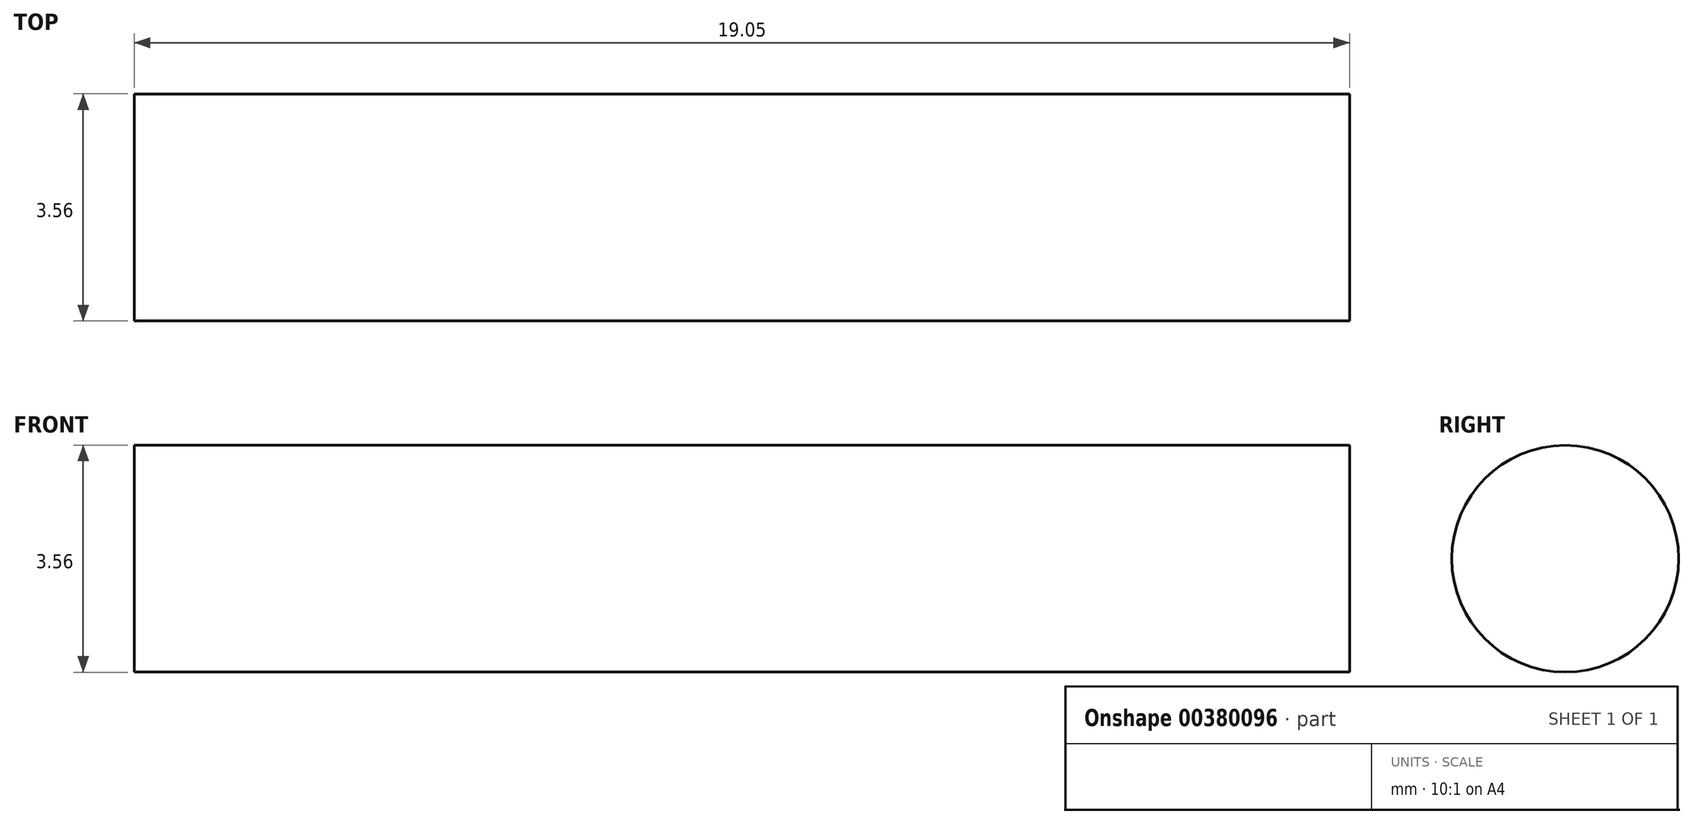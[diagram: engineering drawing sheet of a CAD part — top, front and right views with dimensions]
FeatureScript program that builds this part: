
annotation { "Feature Type Name" : "Feature", "Feature Type Description" : "" }
export const myFeature = defineFeature(function(context is Context, id is Id, definition is map)
    precondition{}
    {
        {
            var Q0;
            Q0=qCreatedBy(makeId("Right.planeOp"),FACE);
            var sketch = newSketch(context, id + "F0", { "sketchPlane" : qUnion([Q0])});
            skCircle(sketch, "E0", {"center": v(0, 0) * mm, "radius": 1.78 * mm});
            skSolve(sketch);
        }
        {
            var Q0;
            Q0 = qSketchRegion(id + "F0", true);
            extrude(context, id + "F1", {"entities" : qUnion([Q0]), "depth" : 19.05 * mm});
        }
    });
